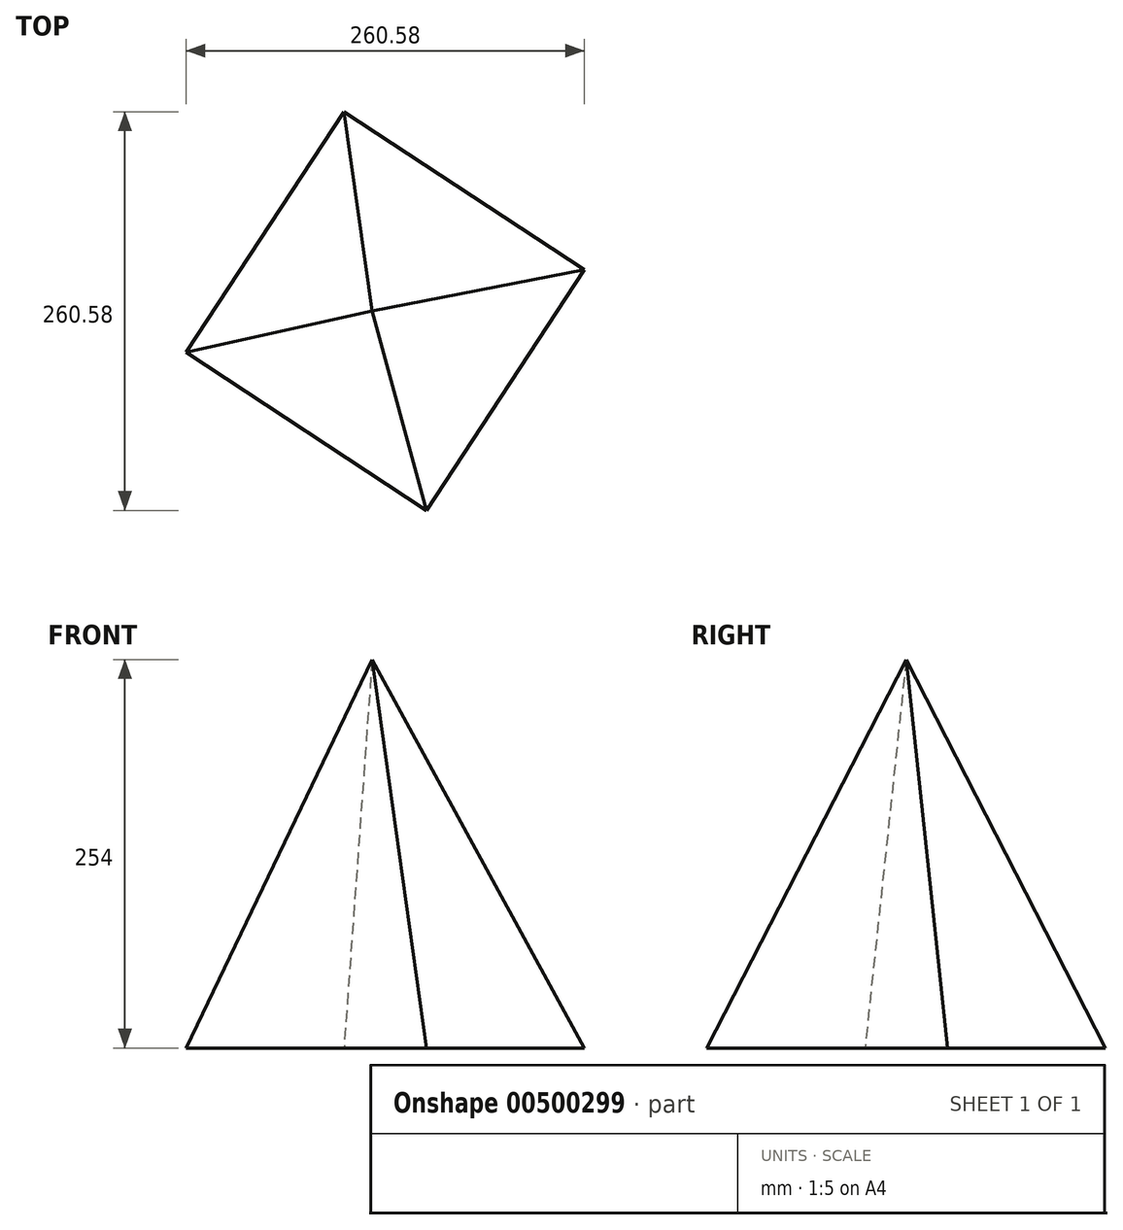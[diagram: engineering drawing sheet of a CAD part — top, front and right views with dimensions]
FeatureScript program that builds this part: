
annotation { "Feature Type Name" : "Feature", "Feature Type Description" : "" }
export const myFeature = defineFeature(function(context is Context, id is Id, definition is map)
    precondition{}
    {
        {
            var Q0;
            Q0=qCreatedBy(makeId("Top.planeOp"),FACE);
            var sketch = newSketch(context, id + "F0", { "sketchPlane" : qUnion([Q0])});
            skCircle(sketch, "E0.cCircle", {"center": v(0, 0) * mm, "radius": 133.05 * mm, "construction": true});
            skLineSegment(sketch, "E0.0", {"start": v(-130.29, -26.96) * mm, "end": v(-26.96, 130.29) * mm});
            skLineSegment(sketch, "E0.1", {"start": v(-26.96, 130.29) * mm, "end": v(130.29, 26.96) * mm});
            skLineSegment(sketch, "E0.2", {"start": v(130.29, 26.96) * mm, "end": v(26.96, -130.29) * mm});
            skLineSegment(sketch, "E0.3", {"start": v(26.96, -130.29) * mm, "end": v(-130.29, -26.96) * mm});
            skSolve(sketch);
        }
        {
            var Q0;
            Q0=qCreatedBy(makeId("Top.planeOp"),FACE);
            cPlane(context, id + "F1", {"entities" : qUnion([Q0]), "cplaneType" : CPlaneType.OFFSET, "offset" : 254 * mm, "width" : 152.4 * mm, "height" : 152.4 * mm});
        }
        {
            var Q0;
            Q0=qCreatedBy(id+"F1.planeOp",FACE);
            var sketch = newSketch(context, id + "F2", { "sketchPlane" : qUnion([Q0])});
            skPoint(sketch, "E1", {"position": v(-8.65, 0) * mm});
            skSolve(sketch);
        }
        {
            var Q0;
            Q0=sQuery(id+"F2.wireOp",VERTEX,"E1");
            var Q1;
            Q1=makeQuery(id+"F0.imprint","IMPRINT",FACE,{"disambiguationData":[TD([[makeQuery(id+"F0.imprint","IMPRINT",EDGE,{"derivedFrom":sQuery(id+"F0.wireOp",EDGE,"E0.0")}),-1.0]])]});
            loft(context, id + "F3", {"sheetProfilesArray" : [{ "sheetProfileEntities" : qUnion([Q0]) }, { "sheetProfileEntities" : qUnion([Q1]) }]});
        }
    });
